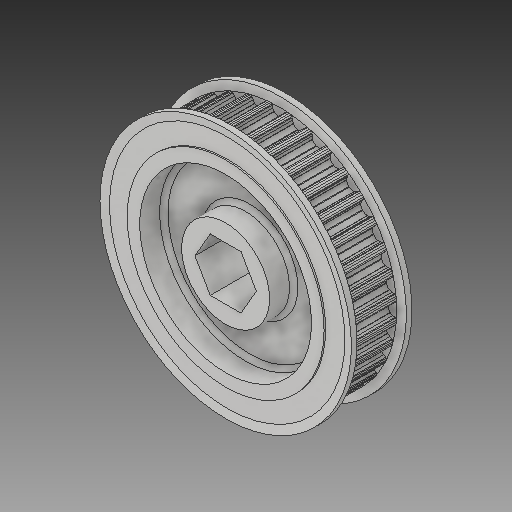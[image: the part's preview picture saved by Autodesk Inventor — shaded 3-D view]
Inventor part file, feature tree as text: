
AUTODESK INVENTOR PART (.ipt)
format: ipt  version: 2017 (Build 210142000, 142)  size: 841,216 bytes
history: native  units: in
note: dims shown in document units (in); Inventor stores cm internally (conversion verified against a paired STEP export)
features: mirror x1
ambient origin geometry x8: Origin, YZ Plane, XZ Plane, XY Plane, X Axis, Y Axis, Z Axis, Center Point
bodies: Solid1 (feature_tree)
feature tree (1):
  mirror  "Mirror1"
